# Revit family: 1Electronics_Community_Biamp_Subwoofer_IS8-118
name_source: partatom
category: Communication Devices
units: mm (PartAtom-declared; Revit-internal decimal feet)

## family parameters
Cut with Voids When Loaded = No
Host = Face
Maintain Annotation Orientation = No
OmniClass Number = 23.85.10.11.14.14.14
OmniClass Title = Loudspeakers
Part Type = Normal
Room Calculation Point = No
Round Connector Dimension = Use Diameter
Shared = No

## types (2) — shared parameters
Continuous Power Handling  Nominal Impedance = Single Amp - 113V, 1600W @ 8 ohms (6400W peak)
Default Elevation = 48 "
Depth = 28.89 "
Description = IS8-118 High Power Single 18-Inch Subwoofer
Environmental = Outdoor: IP55W per IEC 60529 , MIL-STD-810G
Equalized Maximum SPL = Half Space - Peak: 137 dB - Continuous: 131 dB; Whole Space - Peak: 131 dB - Continuous: 125 dB
Equalized Sensitivity = Half Space - 1W: 99 dB - 2.83V: 99 dB; Whole Space - 1W: 93 dB - 2.83V: 93 dB
Height = 19.8 "
Input Connection = Screw terminal blocks (4-position)
Manufacturer = Biamp
Mounting Points = (24) M10 threaded rigging points
Nominal Maximum SPL = Half Space - Peak: 137 dB - Continuous: 131 dB; Whole Space - Peak: 131 dB - Continuous: 125 dB
Nominal Sensitivity = Half Space - 1W: 99 dB - 2.83V: 99 dB; Whole Space - 1W: 93 dB - 2.83V: 93 dB
Operating Environment = Indoor
Operating Mode = Single Amp
Operating Range = 31 Hz to 145 Hz
Product Documentation Link = https://downloads.biamp.com
Product Page URL = https://www.biamp.com
Product data url = https://bimobject.com
Recommended Amplifiers = Single Amp - 1600W - 3200W @ 8 ohms,  (113V - 160V)
Shipping Weight = 112.00 lbf
Transducers = 1 x 18 (457mm) double-treated cone with 4 (102mm) voice coil, triple demodulation rings, neodymium construction
URL = https://www.biamp.com
Weight = 98.00 lbf
Width = 22.1 "

## per-type parameters (varying)
| type | Grill Material | Housing Material |
| IS8-118 B | Biamp - Plastic - Black(Grid) | Biamp - Plastic - Black |
| IS8-118 W | Biamp - Plastic - White(Grid) | Biamp - Plastic - White |

note: column(s) folded — value = type name in every type: Model

## geometry (parser evidence)
native form markers: Sweep x1
no freeform markers — native parametric forms only
